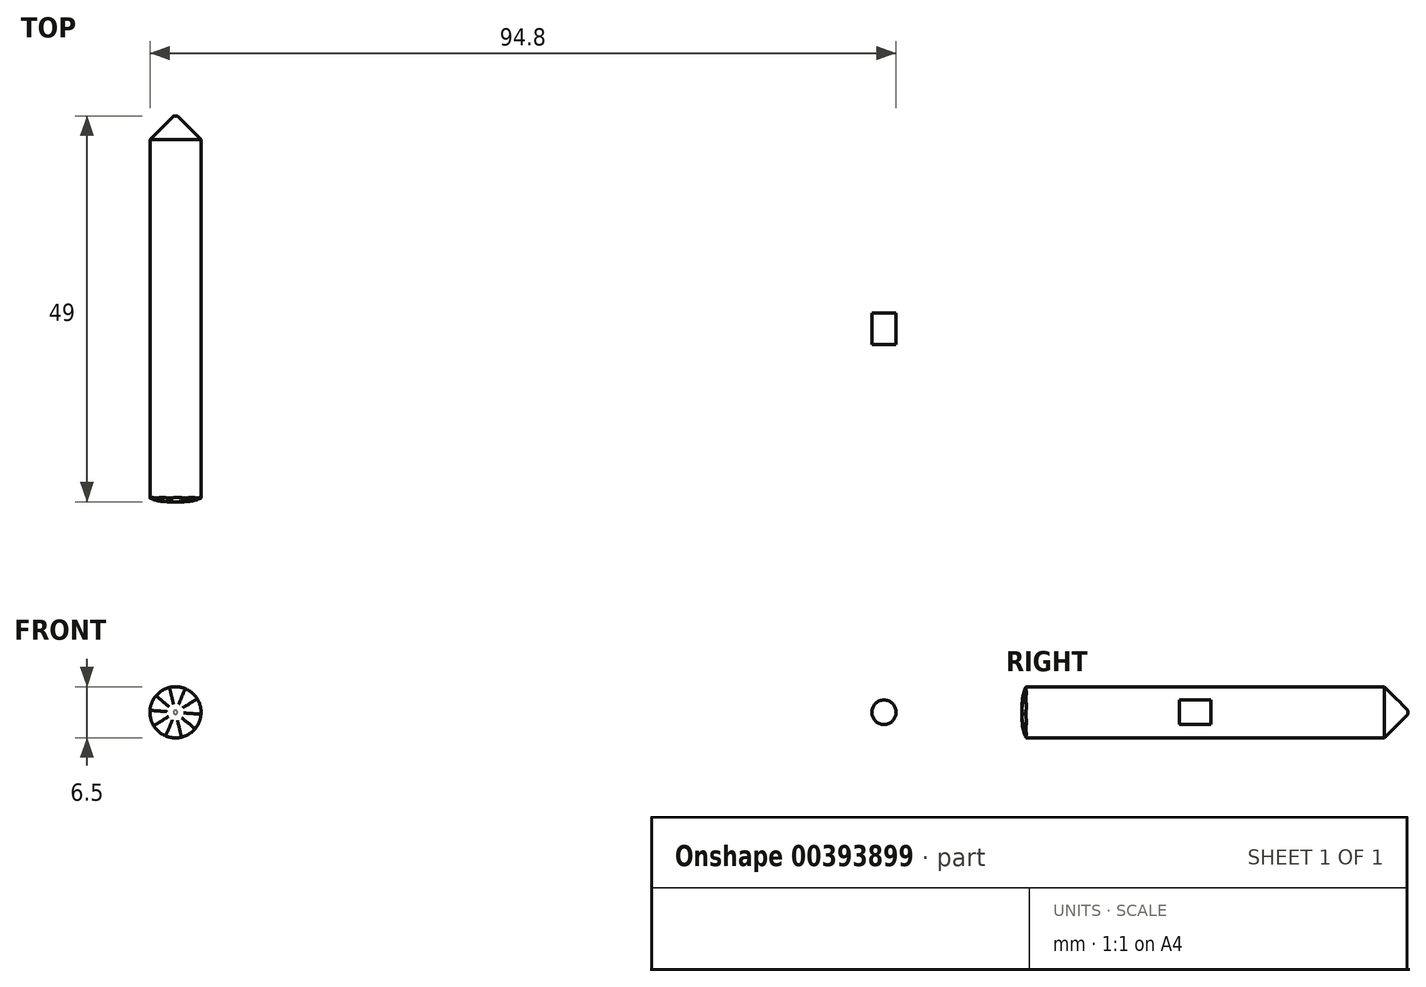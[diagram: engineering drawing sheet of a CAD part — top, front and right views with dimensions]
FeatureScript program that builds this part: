
annotation { "Feature Type Name" : "Feature", "Feature Type Description" : "" }
export const myFeature = defineFeature(function(context is Context, id is Id, definition is map)
    precondition{}
    {
        {
            var Q0;
            Q0=qCreatedBy(makeId("Front.planeOp"),FACE);
            var sketch = newSketch(context, id + "F0", { "sketchPlane" : qUnion([Q0])});
            skLineSegment(sketch, "E0.bottom", {"start": v(-120, 10) * mm, "end": v(120, 10) * mm});
            skLineSegment(sketch, "E0.top", {"start": v(-120, -10) * mm, "end": v(120, -10) * mm});
            skLineSegment(sketch, "E0.left", {"start": v(-120, 10) * mm, "end": v(-120, -10) * mm});
            skLineSegment(sketch, "E0.right", {"start": v(120, 10) * mm, "end": v(120, -10) * mm});
            skPoint(sketch, "E0.middle", {"position": v(0, 0) * mm});
            skSolve(sketch);
        }
        {
            var Q0;
            Q0=makeQuery(id+"F0.imprint","IMPRINT",FACE,{"disambiguationData":[TD([[makeQuery(id+"F0.imprint","IMPRINT",EDGE,{"derivedFrom":sQuery(id+"F0.wireOp",EDGE,"E0.bottom")}),-1.0]])]});
            extrude(context, id + "F1", {"entities" : qUnion([Q0]), "depth" : 4 * mm, "offsetDistance" : 25 * mm});
        }
        {
            var Q0;
            Q0=makeQuery(id+"F1.opExtrude","CAP_FACE",FACE,{"disambiguationData":[OSD([sQuery(id+"F0.wireOp",EDGE,"E0.bottom"),sQuery(id+"F0.wireOp",EDGE,"E0.top"),sQuery(id+"F0.wireOp",EDGE,"E0.left"),sQuery(id+"F0.wireOp",EDGE,"E0.right")])],"isStart":false});
            var sketch = newSketch(context, id + "F2", { "sketchPlane" : qUnion([Q0])});
            skCircle(sketch, "E1", {"center": v(0, 0) * mm, "radius": 6 * mm, "construction": true});
            skLineSegment(sketch, "E2.0", {"start": v(2.4, 5.83) * mm, "end": v(5.37, 3.31) * mm});
            skLineSegment(sketch, "E2.1", {"start": v(5.37, 3.31) * mm, "end": v(6.3, -0.48) * mm});
            skLineSegment(sketch, "E2.2", {"start": v(6.3, -0.48) * mm, "end": v(4.8, -4.08) * mm});
            skLineSegment(sketch, "E2.3", {"start": v(4.8, -4.08) * mm, "end": v(1.49, -6.13) * mm});
            skLineSegment(sketch, "E2.4", {"start": v(1.49, -6.13) * mm, "end": v(-2.4, -5.83) * mm});
            skLineSegment(sketch, "E2.5", {"start": v(-2.4, -5.83) * mm, "end": v(-5.37, -3.31) * mm});
            skLineSegment(sketch, "E2.6", {"start": v(-5.37, -3.31) * mm, "end": v(-6.3, 0.48) * mm});
            skLineSegment(sketch, "E2.7", {"start": v(-6.3, 0.48) * mm, "end": v(-4.8, 4.08) * mm});
            skLineSegment(sketch, "E2.8", {"start": v(-4.8, 4.08) * mm, "end": v(-1.49, 6.13) * mm});
            skLineSegment(sketch, "E2.9", {"start": v(-1.49, 6.13) * mm, "end": v(2.4, 5.83) * mm});
            skPoint(sketch, "E2.0.midPoint", {"position": v(3.88, 4.57) * mm});
            skSolve(sketch);
        }
        {
            var Q0;
            Q0=makeQuery(id+"F2.imprint","IMPRINT",FACE,{"disambiguationData":[TD([[makeQuery(id+"F2.imprint","IMPRINT",EDGE,{"derivedFrom":sQuery(id+"F2.wireOp",EDGE,"E2.0")}),-1.0]])]});
            extrude(context, id + "F3", {"entities" : qUnion([Q0]), "operationType" : NewBodyOperationType.ADD, "depth" : 20 * mm, "offsetDistance" : 25 * mm});
        }
        {
            var Q0;
            Q0=makeQuery(id+"F3.opExtrude","CAP_FACE",FACE,{"disambiguationData":[OSD([sQuery(id+"F2.wireOp",EDGE,"E2.0"),sQuery(id+"F2.wireOp",EDGE,"E2.1"),sQuery(id+"F2.wireOp",EDGE,"E2.2"),sQuery(id+"F2.wireOp",EDGE,"E2.3"),sQuery(id+"F2.wireOp",EDGE,"E2.4"),sQuery(id+"F2.wireOp",EDGE,"E2.5"),sQuery(id+"F2.wireOp",EDGE,"E2.6"),sQuery(id+"F2.wireOp",EDGE,"E2.7"),sQuery(id+"F2.wireOp",EDGE,"E2.8"),sQuery(id+"F2.wireOp",EDGE,"E2.9")])],"isStart":false});
            fillet(context, id + "F4", {"entities" : qUnion([Q0]), "radius" : 5 * mm, "tangentPropagation" : true, "allowEdgeOverflow" : false});
        }
        {
            var Q0;
            Q0=makeQuery(id+"F1.opExtrude","CAP_FACE",FACE,{"disambiguationData":[OSD([sQuery(id+"F0.wireOp",EDGE,"E0.bottom"),sQuery(id+"F0.wireOp",EDGE,"E0.top"),sQuery(id+"F0.wireOp",EDGE,"E0.left"),sQuery(id+"F0.wireOp",EDGE,"E0.right")])],"isStart":true});
            var sketch = newSketch(context, id + "F5", { "sketchPlane" : qUnion([Q0])});
            skCircle(sketch, "E3", {"center": v(0, 0) * mm, "radius": 3.25 * mm});
            skSolve(sketch);
        }
        {
            var Q0;
            Q0=makeQuery(id+"F5.imprint","IMPRINT",FACE,{"disambiguationData":[TD([[makeQuery(id+"F5.imprint","IMPRINT",EDGE,{"derivedFrom":sQuery(id+"F5.wireOp",EDGE,"E3")}),1.0]])]});
            extrude(context, id + "F6", {"entities" : qUnion([Q0]), "operationType" : NewBodyOperationType.ADD, "depth" : 25 * mm, "offsetDistance" : 25 * mm});
        }
        {
            var Q0;
            Q0=makeQuery(id+"F6.opExtrude","CAP_FACE",FACE,{"disambiguationData":[OSD([sQuery(id+"F5.wireOp",EDGE,"E3")])],"isStart":false});
            chamfer(context, id + "F7", {"entities" : qUnion([Q0]), "width" : 3 * mm, "tangentPropagation" : true});
        }
        {
            var Q0;
            Q0=makeQuery(id+"F1.opExtrude","CAP_FACE",FACE,{"disambiguationData":[OSD([sQuery(id+"F0.wireOp",EDGE,"E0.bottom"),sQuery(id+"F0.wireOp",EDGE,"E0.top"),sQuery(id+"F0.wireOp",EDGE,"E0.left"),sQuery(id+"F0.wireOp",EDGE,"E0.right")])],"isStart":true});
            var sketch = newSketch(context, id + "F8", { "sketchPlane" : qUnion([Q0])});
            skCircle(sketch, "E4", {"center": v(90, 0) * mm, "radius": 1.55 * mm});
            skCircle(sketch, "E5.MirrorC", {"center": v(-90, 0) * mm, "radius": 1.55 * mm});
            skSolve(sketch);
        }
        {
            var Q0;
            Q0=makeQuery(id+"F8.imprint","IMPRINT",FACE,{"disambiguationData":[TD([[makeQuery(id+"F8.imprint","IMPRINT",EDGE,{"derivedFrom":sQuery(id+"F8.wireOp",EDGE,"E5.MirrorC")}),-1.0]])]});
            var Q1;
            Q1=makeQuery(id+"F8.imprint","IMPRINT",FACE,{"disambiguationData":[TD([[makeQuery(id+"F8.imprint","IMPRINT",EDGE,{"derivedFrom":sQuery(id+"F8.wireOp",EDGE,"E4")}),1.0]])]});
            extrude(context, id + "F9", {"entities" : qUnion([Q0, Q1]), "operationType" : NewBodyOperationType.REMOVE, "oppositeDirection" : true, "depth" : 25 * mm, "offsetDistance" : 25 * mm});
        }
    });
